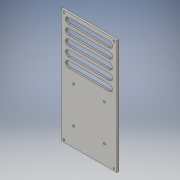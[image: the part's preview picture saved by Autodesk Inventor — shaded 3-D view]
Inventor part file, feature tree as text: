
AUTODESK INVENTOR PART (.ipt)
format: ipt  version: 2016 (Build 200138000, 138)  size: 151,040 bytes
history: native  units: mm
features: sketch x3, extrude x2, hole x2, mirror x2, pattern_linear x1
ambient origin geometry x8: Origin, YZ Plane, XZ Plane, XY Plane, X Axis, Y Axis, Z Axis, Center Point
bodies: Volumenkörper1 (feature_tree)
feature tree (10):
  extrude  "Extrusion1"  Depth=182.6mm
  hole  "Bohrung1"  [1 undecoded]
  extrude  "Extrusion2"  Depth=30.0mm
  pattern_linear  "Rechteckige Anordnung1"  Spacing1=75.0mm  [1 undecoded]
  hole  "Bohrung2"  [1 undecoded]
  mirror  "Spiegeln1"
  mirror  "Spiegeln2"
  sketch  "Skizze1"  dims[d0=88.6mm d1=182.6mm]
  sketch  "Skizze2"  dims[d2=3.0mm d3=0.0mm d5=49.0mm]
  sketch  "Skizze3"  dims[d6=58.0mm d7=30.0mm d8=3.0mm d9=6.0mm d10=4.0mm d11=2.0mm d12=90.0deg d13=2.5mm d14=0.0mm d15=75.0mm d16=10.0mm d18=5.0mm d19=5.0mm d20=5.0mm d21=10.0mm d22=0.0mm d23=50.0mm d25=15.0mm d26=4.4mm d27=3.4mm d28=3.0mm d29=6.0mm d30=4.0mm d31=2.0mm d32=90.0deg d33=8.0mm d34=20.594885mm]
note: 3 required parameter values undecoded (feature->parameter linkage not recoverable at this tier; creation-order binding heuristic only, values carry confidence <= 0.55)
